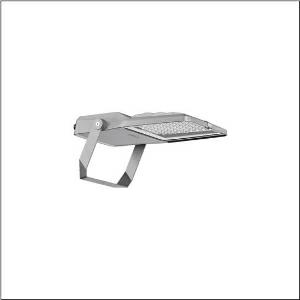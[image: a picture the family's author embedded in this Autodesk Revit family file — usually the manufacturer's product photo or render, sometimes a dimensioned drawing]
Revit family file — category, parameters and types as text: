
# Revit family: floodlight_fl_21_mini___pl43_5xa7776b2a1a_e86b
name_source: partatom
category: Lighting Fixtures
units: mm (PartAtom-declared; Revit-internal decimal feet)

## family parameters
Cut with Voids When Loaded = No
Host = Face
Light Source = No
Part Type = Normal
Room Calculation Point = No
Round Connector Dimension = Use Diameter
Shared = No

## types (1)
- --- (1 x LED, 6390 lm, 45.7 W, 3000K)
    Apparent Load = 46 VA
    CIE Flux Codes = 27 78 99 100 100
    Color Rendering = 70
    Color Temperature = 3000K
    Default Elevation = 1800 mm
    Description = Floodlight FL 21 mini, floodlight, primary light control with lens, of PMMA, primary optical cover: protective disc, of toughened safety glass, transparent, light distribution: PL43, light emission: direct distribution, installation type: surface-mounted, LED, High Power LED, rated luminous flux: 6.390lm, luminous efficacy: 140lm/W, light colour: 730, colour temperature: 3000K, control gear: Smart Interface (Zhaga), control: flexible luminous flux parameterisation, time-dependent luminous flux control, constant luminous flux control, overheat protection, pre-setting: logarithmic dimming characteristic, with terminal, 6-pole, mains connection: 220..240V, AC, 50/60Hz, start of lifetime: 46W, end of service life: 48W, reduction: 22W, luminaire housing, of diecast aluminium, powder-coated, Siteco® metallic grey (DB 702S), corrosivity category C5 mid according to DIN EN ISO 12944, suitable for swimming pools, chlorine-resistant, sealing non-destructively replaceable, mounting bracket, of steel, galvanised, powder-coated, Siteco® metallic grey (DB 702S), Smart Interface below and above, protection rating (complete): IP66, insulation class (complete): insulation class II (safety insulation), certification: CE, ENEC, VDE, protection symbol: D, impact resistance: IK08, permissible operating ambient temperature: -40..+40°C, permissible operating ambient temperature for outdoor applications: -40..+50°C, standard: DIN EN 12944, LABS conformity tested according to VDMA 24364:2018-05, packaging unit: 1 piece

Light Distribution: PL43
    Height = 70 mm
    Lamp = 1 x LED
    Lamp Light Flux = 6390 lm
    Lamp Power = 45.7 W
    Lamp count = 1
    Length = 485 mm
    Luminous efficacy = 140 lm/W
    Manufacturer = Siteco
    ModVariant = No
    Model = 5XA7776B2A1A
    Number of Poles = 1
    OnlyDefault = Yes
    Power Factor = 1
    Product Name = Floodlight FL 21 mini | PL43
    Product group = floodlight | pylon annexe
    ProductGroupID = 6200
    Protection Class = Protection class II
    Protection Degree = IP 66
    RLX_Detail_Level = 1
    RLX_Emergency_Light_Flux = 0 lm
    RLX_Emergency_Type = 0
    RLX_Emergency_Type_DB = No
    RlxData = <blob elided: 95925 chars, md5=be77ccfe>
    Socket = socket
    Standby Power = 0 W
    System Light Flux = 6390 lm
    System Power = 46 W
    Type Comments = factory setting: luminous flux: 100 % | dim-lin: 254 | 463 mA
    Type Image = l_1006845.jpg
    URL = http://relux.com
    VarID = @adj_161292
    Voltage = 0 V
    Weight = 0.00 kg
    Width = 337 mm

## geometry (parser evidence)
native form markers: Blend x4, Sweep x12
no freeform markers — native parametric forms only
